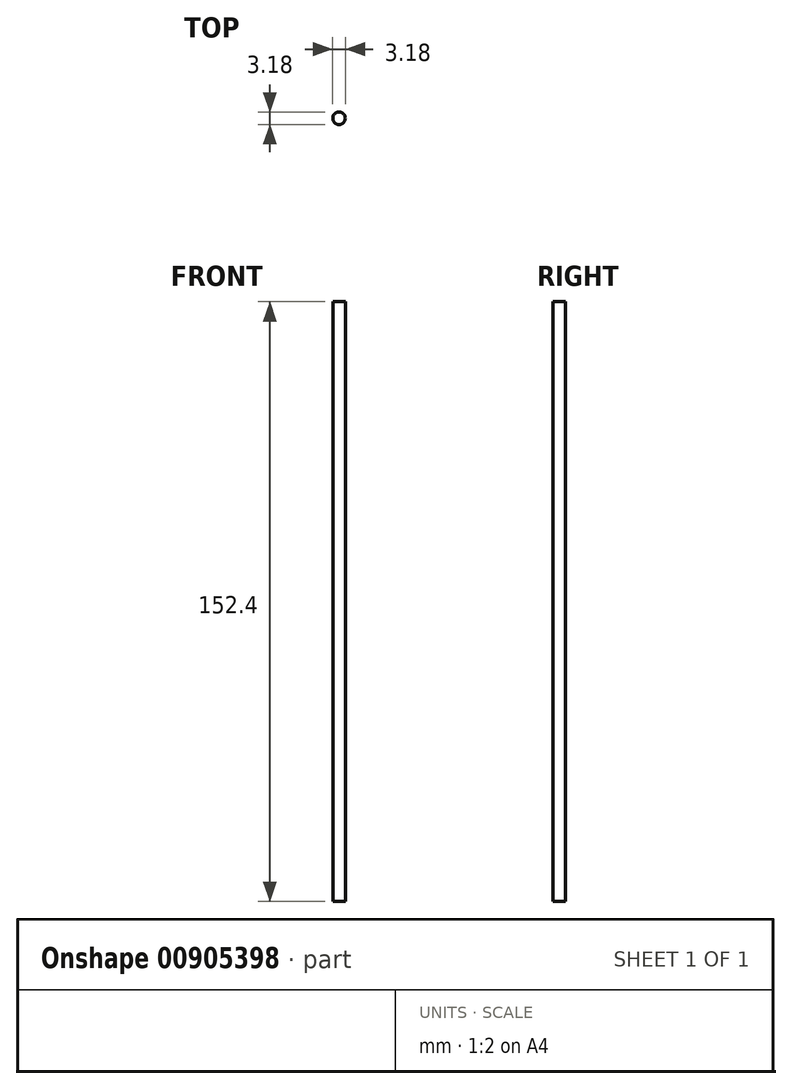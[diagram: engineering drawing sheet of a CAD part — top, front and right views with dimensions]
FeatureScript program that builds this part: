
annotation { "Feature Type Name" : "Feature", "Feature Type Description" : "" }
export const myFeature = defineFeature(function(context is Context, id is Id, definition is map)
    precondition{}
    {
        {
            var Q0;
            Q0=qCreatedBy(makeId("Top.planeOp"),FACE);
            var sketch = newSketch(context, id + "F0", { "sketchPlane" : qUnion([Q0])});
            skCircle(sketch, "E0", {"center": v(0, 0) * mm, "radius": 1.59 * mm});
            skSolve(sketch);
        }
        {
            var Q0;
            Q0 = qSketchRegion(id + "F0", true);
            extrude(context, id + "F1", {"entities" : qUnion([Q0]), "endBound" : BoundingType.SYMMETRIC, "depth" : 127 * mm, "offsetDistance" : 25.4 * mm});
        }
        {
            var Q0;
            Q0=makeQuery(id+"F1.opExtrude","CAP_FACE",FACE,{"disambiguationData":[OSD([sQuery(id+"F0.wireOp",EDGE,"E0")])],"isStart":false});
            extrude(context, id + "F2", {"entities" : qUnion([Q0]), "operationType" : NewBodyOperationType.ADD, "depth" : 25.4 * mm, "offsetDistance" : 25.4 * mm});
        }
    });
